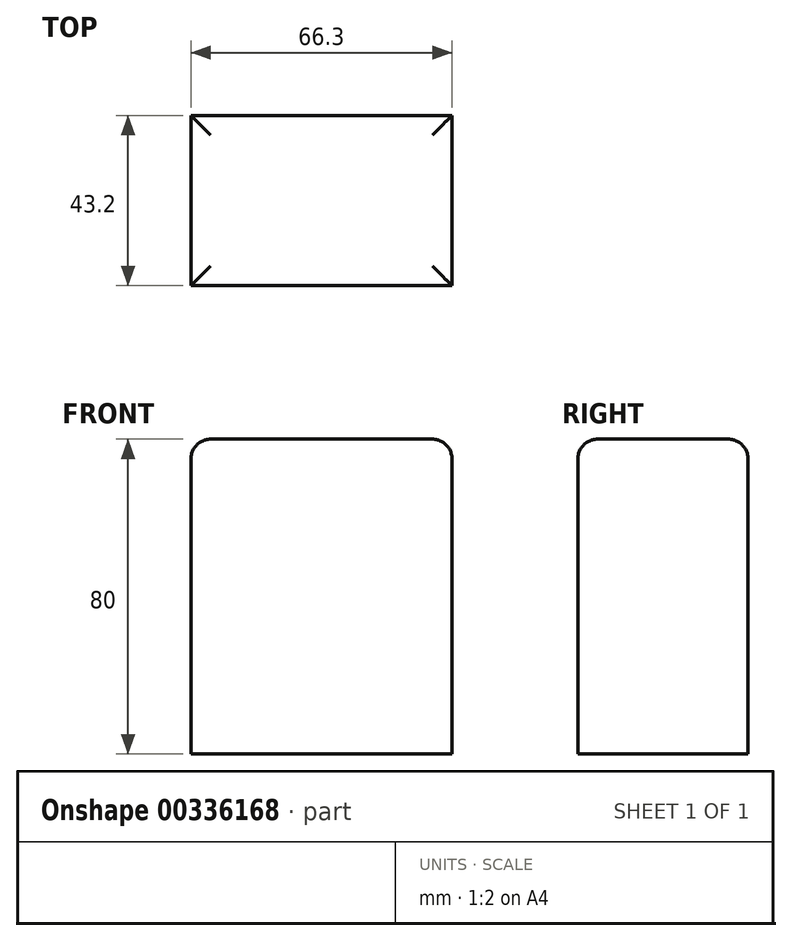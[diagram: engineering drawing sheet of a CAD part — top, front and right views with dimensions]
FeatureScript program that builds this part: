
annotation { "Feature Type Name" : "Feature", "Feature Type Description" : "" }
export const myFeature = defineFeature(function(context is Context, id is Id, definition is map)
    precondition{}
    {
        {
            var Q0;
            Q0=qCreatedBy(makeId("Top.planeOp"),FACE);
            var sketch = newSketch(context, id + "F0", { "sketchPlane" : qUnion([Q0])});
            skLineSegment(sketch, "E0.bottom", {"start": v(-32.7, 21.75) * mm, "end": v(33.6, 21.75) * mm});
            skLineSegment(sketch, "E0.top", {"start": v(-32.7, -21.45) * mm, "end": v(33.6, -21.45) * mm});
            skLineSegment(sketch, "E0.left", {"start": v(-32.7, 21.75) * mm, "end": v(-32.7, -21.45) * mm});
            skLineSegment(sketch, "E0.right", {"start": v(33.6, 21.75) * mm, "end": v(33.6, -21.45) * mm});
            skSolve(sketch);
        }
        {
            var Q0;
            Q0=makeQuery(id+"F0.imprint","IMPRINT",FACE,{"disambiguationData":[TD([[makeQuery(id+"F0.imprint","IMPRINT",EDGE,{"derivedFrom":sQuery(id+"F0.wireOp",EDGE,"E0.bottom")}),-1.0]])]});
            extrude(context, id + "F1", {"entities" : qUnion([Q0]), "endBound" : BoundingType.SYMMETRIC, "depth" : 80 * mm});
        }
        {
            var Q0;
            Q0=makeQuery(id+"F1.opExtrude","CAP_FACE",FACE,{"disambiguationData":[OSD([sQuery(id+"F0.wireOp",EDGE,"E0.bottom"),sQuery(id+"F0.wireOp",EDGE,"E0.top"),sQuery(id+"F0.wireOp",EDGE,"E0.left"),sQuery(id+"F0.wireOp",EDGE,"E0.right")])],"isStart":false});
            fillet(context, id + "F2", {"entities" : qUnion([Q0]), "radius" : 5 * mm, "tangentPropagation" : true, "allowEdgeOverflow" : false});
        }
    });
